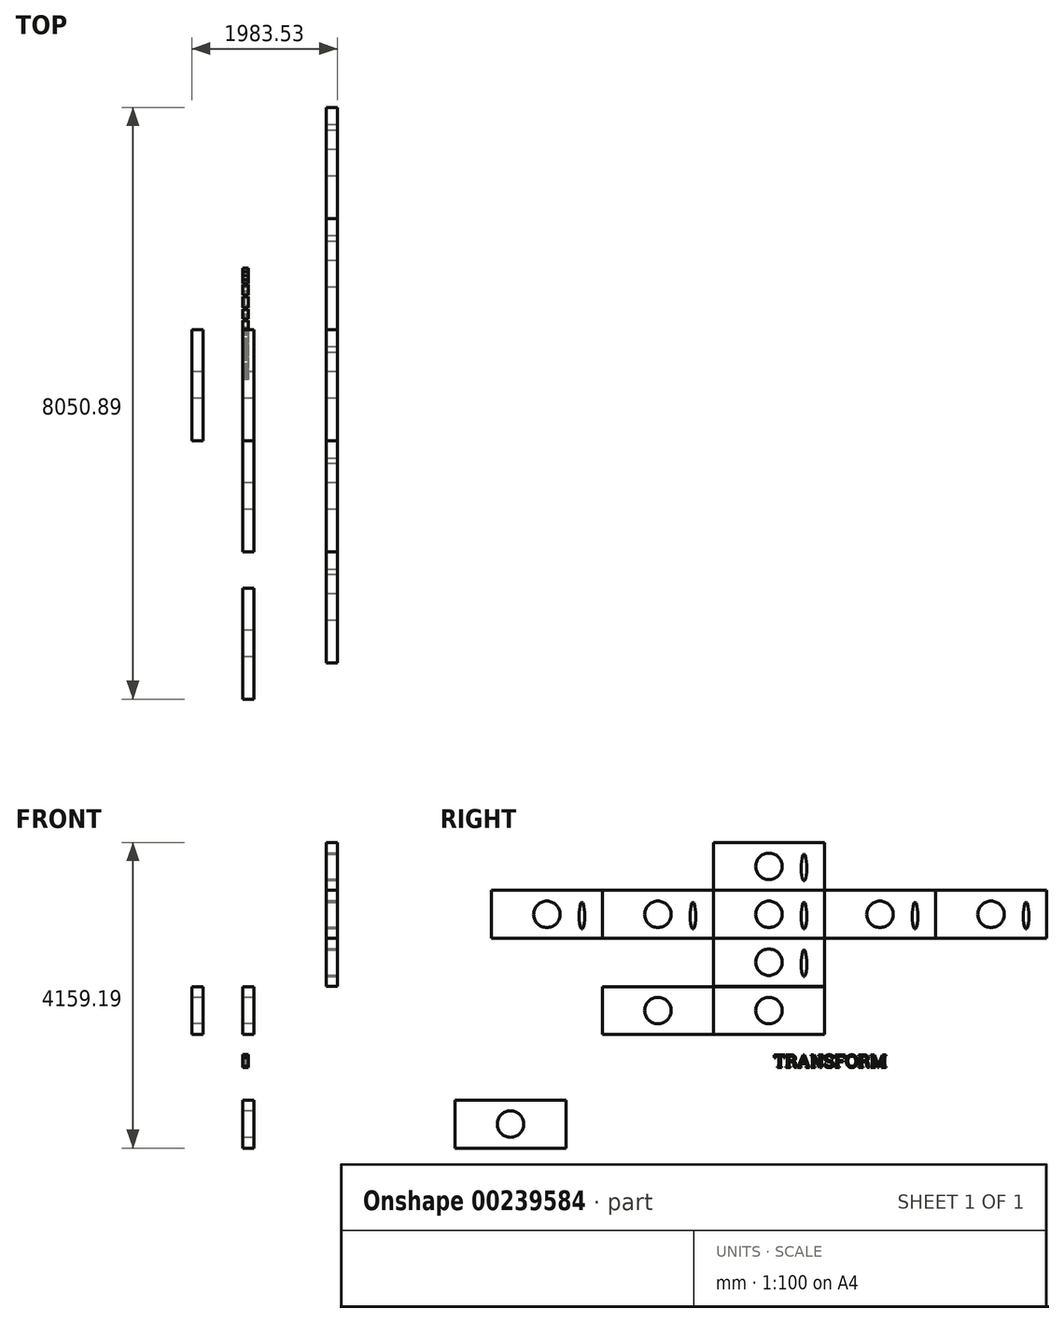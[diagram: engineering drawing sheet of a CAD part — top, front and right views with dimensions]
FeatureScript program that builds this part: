
annotation { "Feature Type Name" : "Feature", "Feature Type Description" : "" }
export const myFeature = defineFeature(function(context is Context, id is Id, definition is map)
    precondition{}
    {
        {
            var Q0;
            Q0=qCreatedBy(makeId("Right.planeOp"),FACE);
            var sketch = newSketch(context, id + "F0", { "sketchPlane" : qUnion([Q0])});
            skText(sketch, "E0", { "text": "TRANSFORM", "fontName": "RobotoSlab-Regular.ttf"});
            const initialGuessF0  = {"E0": [0.06953, -0.13173, 1, 0, 0.17393]};
            skSetInitialGuess(sketch, initialGuessF0);
            skSolve(sketch);
        }
        {
            var Q0;
            Q0=makeQuery(id+"F0.imprint","IMPRINT",FACE,{"disambiguationData":[TD([[makeQuery(id+"F0.imprint","IMPRINT",EDGE,{"derivedFrom":sQuery(id+"F0.wireOp",EDGE,"E0.sketch_text.stroke-154")}),1.0]])]});
            extrude(context, id + "F1", {"entities" : qUnion([Q0]), "depth" : 25.4 * mm});
        }
        {
            var Q0;
            Q0 = qSketchRegion(id + "F0", true);
            extrude(context, id + "F2", {"entities" : qUnion([Q0]), "operationType" : NewBodyOperationType.ADD, "depth" : 81.53 * mm});
        }
        {
            var Q0;
            Q0=qCreatedBy(makeId("Right.planeOp"),FACE);
            var sketch = newSketch(context, id + "F3", { "sketchPlane" : qUnion([Q0])});
            skLineSegment(sketch, "E1.bottom", {"start": v(755.67, 317.14) * mm, "end": v(-755.67, 317.14) * mm});
            skLineSegment(sketch, "E1.top", {"start": v(755.67, 969.35) * mm, "end": v(-755.67, 969.35) * mm});
            skLineSegment(sketch, "E1.left", {"start": v(755.67, 317.14) * mm, "end": v(755.67, 969.35) * mm});
            skLineSegment(sketch, "E1.right", {"start": v(-755.67, 317.14) * mm, "end": v(-755.67, 969.35) * mm});
            skPoint(sketch, "E1.middle", {"position": v(0, 643.24) * mm});
            skCircle(sketch, "E2", {"center": v(0, 643.24) * mm, "radius": 180.1 * mm});
            skSolve(sketch);
        }
        {
            var Q0;
            Q0 = qSketchRegion(id + "F3", true);
            extrude(context, id + "F14", {"entities" : qUnion([Q0]), "depth" : 152.9 * mm});
        }
        {
            var Q0;
            Q0=makeQuery(id+"F14.opExtrude","SWEPT_BODY",BODY,{"disambiguationData":[OSD([sQuery(id+"F3.wireOp",EDGE,"E1.bottom"),sQuery(id+"F3.wireOp",EDGE,"E1.top"),sQuery(id+"F3.wireOp",EDGE,"E1.left"),sQuery(id+"F3.wireOp",EDGE,"E1.right"),sQuery(id+"F3.wireOp",EDGE,"E2")])]});
            var Q1;
            Q1=sQuery(id+"F3.wireOp",EDGE,"E1.top");
            transform(context, id + "F4", {"entities" : qUnion([Q0]), "transformType" : TransformType.TRANSLATION_ENTITY, "oppositeDirectionEntity" : false, "transformLine" : qUnion([Q1]), "makeCopy" : true});
        }
        {
            var Q0;
            Q0=makeQuery(id+"F14.opExtrude","SWEPT_BODY",BODY,{"disambiguationData":[OSD([sQuery(id+"F3.wireOp",EDGE,"E1.bottom"),sQuery(id+"F3.wireOp",EDGE,"E1.top"),sQuery(id+"F3.wireOp",EDGE,"E1.left"),sQuery(id+"F3.wireOp",EDGE,"E1.right"),sQuery(id+"F3.wireOp",EDGE,"E2")])]});
            var Q1;
            Q1=sQuery(id+"F3.wireOp",EDGE,"E1.top");
            transform(context, id + "F15", {"entities" : qUnion([Q0]), "transformType" : TransformType.TRANSLATION_ENTITY, "oppositeDirectionEntity" : false, "transformLine" : qUnion([Q1]), "makeCopy" : true});
        }
        {
            var Q0;
            Q0=makeQuery(id+"F14.opExtrude","SWEPT_BODY",BODY,{"disambiguationData":[OSD([sQuery(id+"F3.wireOp",EDGE,"E1.bottom"),sQuery(id+"F3.wireOp",EDGE,"E1.top"),sQuery(id+"F3.wireOp",EDGE,"E1.left"),sQuery(id+"F3.wireOp",EDGE,"E1.right"),sQuery(id+"F3.wireOp",EDGE,"E2")])]});
            var Q1;
            Q1=makeQuery(id+"F14.opExtrude","CAP_EDGE",EDGE,{"disambiguationData":[OSD([sQuery(id+"F3.wireOp",EDGE,"E1.top")])],"isStart":false});
            transform(context, id + "F5", {"entities" : qUnion([Q0]), "transformType" : TransformType.TRANSLATION_3D, "dx" : -692.43 * mm, "dy" : 0 * mm, "dz" : 0 * mm, "makeCopy" : true});
        }
        {
            var Q0;
            Q0=makeQuery(id+"F14.opExtrude","SWEPT_BODY",BODY,{"disambiguationData":[OSD([sQuery(id+"F3.wireOp",EDGE,"E1.bottom"),sQuery(id+"F3.wireOp",EDGE,"E1.top"),sQuery(id+"F3.wireOp",EDGE,"E1.left"),sQuery(id+"F3.wireOp",EDGE,"E1.right"),sQuery(id+"F3.wireOp",EDGE,"E2")])]});
            transform(context, id + "F16", {"entities" : qUnion([Q0]), "transformType" : TransformType.TRANSLATION_3D, "dx" : 1138.2 * mm, "dy" : 0 * mm, "dz" : 1309.2 * mm, "makeCopy" : true});
        }
        {
            var Q0;
            Q0=makeQuery(id+"F16.opPattern","COPY",FACE,{"derivedFrom":makeQuery(id+"F14.opExtrude","CAP_FACE",FACE,{"disambiguationData":[OSD([sQuery(id+"F3.wireOp",EDGE,"E1.bottom"),sQuery(id+"F3.wireOp",EDGE,"E1.top"),sQuery(id+"F3.wireOp",EDGE,"E1.left"),sQuery(id+"F3.wireOp",EDGE,"E1.right"),sQuery(id+"F3.wireOp",EDGE,"E2")])],"isStart":false}),"instanceName":"1"});
            var sketch = newSketch(context, id + "F6", { "sketchPlane" : qUnion([Q0])});
            skEllipse(sketch, "E3", {"center": v(477.82, 1935.9) * mm, "majorRadius": 181.6 * mm, "minorRadius": 37.73 * mm, "majorAxis": v(0, 1)});
            skSolve(sketch);
        }
        {
            var Q0;
            Q0 = qSketchRegion(id + "F6", true);
            extrude(context, id + "F7", {"entities" : qUnion([Q0]), "operationType" : NewBodyOperationType.REMOVE, "endBound" : BoundingType.THROUGH_ALL, "oppositeDirection" : true, "depth" : 25.4 * mm});
        }
        {
            var Q0;
            Q0=makeQuery(id+"F16.opPattern","COPY",BODY,{"derivedFrom":makeQuery(id+"F14.opExtrude","SWEPT_BODY",BODY,{"disambiguationData":[OSD([sQuery(id+"F3.wireOp",EDGE,"E1.bottom"),sQuery(id+"F3.wireOp",EDGE,"E1.top"),sQuery(id+"F3.wireOp",EDGE,"E1.left"),sQuery(id+"F3.wireOp",EDGE,"E1.right"),sQuery(id+"F3.wireOp",EDGE,"E2")])]}),"instanceName":"1"});
            var Q1;
            Q1=makeQuery(id+"F16.opPattern","COPY",EDGE,{"derivedFrom":makeQuery(id+"F14.opExtrude","CAP_EDGE",EDGE,{"disambiguationData":[OSD([sQuery(id+"F3.wireOp",EDGE,"E1.top")])],"isStart":false}),"instanceName":"1"});
            transform(context, id + "F8", {"entities" : qUnion([Q0]), "transformType" : TransformType.TRANSLATION_ENTITY, "oppositeDirectionEntity" : false, "transformLine" : qUnion([Q1]), "makeCopy" : true});
        }
        {
            var Q0;
            Q0=makeQuery(id+"F4.opPattern","COPY",BODY,{"derivedFrom":makeQuery(id+"F14.opExtrude","SWEPT_BODY",BODY,{"disambiguationData":[OSD([sQuery(id+"F3.wireOp",EDGE,"E1.bottom"),sQuery(id+"F3.wireOp",EDGE,"E1.top"),sQuery(id+"F3.wireOp",EDGE,"E1.left"),sQuery(id+"F3.wireOp",EDGE,"E1.right"),sQuery(id+"F3.wireOp",EDGE,"E2")])]}),"instanceName":"1"});
            transform(context, id + "F9", {"entities" : qUnion([Q0]), "transformType" : TransformType.TRANSLATION_3D, "dx" : 0 * mm, "dy" : -2005.56 * mm, "dz" : -1545.56 * mm, "makeCopy" : true});
        }
        {
            var Q0;
            Q0=makeQuery(id+"F16.opPattern","COPY",BODY,{"derivedFrom":makeQuery(id+"F14.opExtrude","SWEPT_BODY",BODY,{"disambiguationData":[OSD([sQuery(id+"F3.wireOp",EDGE,"E1.bottom"),sQuery(id+"F3.wireOp",EDGE,"E1.top"),sQuery(id+"F3.wireOp",EDGE,"E1.left"),sQuery(id+"F3.wireOp",EDGE,"E1.right"),sQuery(id+"F3.wireOp",EDGE,"E2")])]}),"instanceName":"1"});
            var Q1;
            Q1=makeQuery(id+"F16.opPattern","COPY",EDGE,{"derivedFrom":makeQuery(id+"F14.opExtrude","CAP_EDGE",EDGE,{"disambiguationData":[OSD([sQuery(id+"F3.wireOp",EDGE,"E1.left")])],"isStart":false}),"instanceName":"1"});
            transform(context, id + "F17", {"entities" : qUnion([Q0]), "transformType" : TransformType.TRANSLATION_ENTITY, "oppositeDirectionEntity" : false, "transformLine" : qUnion([Q1]), "makeCopy" : true});
        }
        {
            var Q0;
            Q0=makeQuery(id+"F16.opPattern","COPY",BODY,{"derivedFrom":makeQuery(id+"F14.opExtrude","SWEPT_BODY",BODY,{"disambiguationData":[OSD([sQuery(id+"F3.wireOp",EDGE,"E1.bottom"),sQuery(id+"F3.wireOp",EDGE,"E1.top"),sQuery(id+"F3.wireOp",EDGE,"E1.left"),sQuery(id+"F3.wireOp",EDGE,"E1.right"),sQuery(id+"F3.wireOp",EDGE,"E2")])]}),"instanceName":"1"});
            var Q1;
            Q1=makeQuery(id+"F16.opPattern","COPY",EDGE,{"derivedFrom":makeQuery(id+"F14.opExtrude","CAP_EDGE",EDGE,{"disambiguationData":[OSD([sQuery(id+"F3.wireOp",EDGE,"E1.left")])],"isStart":false}),"instanceName":"1"});
            transform(context, id + "F10", {"entities" : qUnion([Q0]), "transformType" : TransformType.TRANSLATION_ENTITY, "oppositeDirectionEntity" : true, "transformLine" : qUnion([Q1]), "makeCopy" : true});
        }
        {
            var Q0;
            Q0=makeQuery(id+"F16.opPattern","COPY",BODY,{"derivedFrom":makeQuery(id+"F14.opExtrude","SWEPT_BODY",BODY,{"disambiguationData":[OSD([sQuery(id+"F3.wireOp",EDGE,"E1.bottom"),sQuery(id+"F3.wireOp",EDGE,"E1.top"),sQuery(id+"F3.wireOp",EDGE,"E1.left"),sQuery(id+"F3.wireOp",EDGE,"E1.right"),sQuery(id+"F3.wireOp",EDGE,"E2")])]}),"instanceName":"1"});
            var Q1;
            Q1=makeQuery(id+"F16.opPattern","COPY",EDGE,{"derivedFrom":makeQuery(id+"F14.opExtrude","CAP_EDGE",EDGE,{"disambiguationData":[OSD([sQuery(id+"F3.wireOp",EDGE,"E1.bottom")])],"isStart":false}),"instanceName":"1"});
            transform(context, id + "F11", {"entities" : qUnion([Q0]), "transformType" : TransformType.TRANSLATION_ENTITY, "oppositeDirectionEntity" : true, "transformLine" : qUnion([Q1]), "makeCopy" : true});
        }
        {
            var Q0;
            Q0=makeQuery(id+"F11.opPattern","COPY",BODY,{"derivedFrom":makeQuery(id+"F16.opPattern","COPY",BODY,{"derivedFrom":makeQuery(id+"F14.opExtrude","SWEPT_BODY",BODY,{"disambiguationData":[OSD([sQuery(id+"F3.wireOp",EDGE,"E1.bottom"),sQuery(id+"F3.wireOp",EDGE,"E1.top"),sQuery(id+"F3.wireOp",EDGE,"E1.left"),sQuery(id+"F3.wireOp",EDGE,"E1.right"),sQuery(id+"F3.wireOp",EDGE,"E2")])]}),"instanceName":"1"}),"instanceName":"1"});
            var Q1;
            Q1=makeQuery(id+"F11.opPattern","COPY",EDGE,{"derivedFrom":makeQuery(id+"F16.opPattern","COPY",EDGE,{"derivedFrom":makeQuery(id+"F14.opExtrude","CAP_EDGE",EDGE,{"disambiguationData":[OSD([sQuery(id+"F3.wireOp",EDGE,"E1.bottom")])],"isStart":false}),"instanceName":"1"}),"instanceName":"1"});
            transform(context, id + "F12", {"entities" : qUnion([Q0]), "transformType" : TransformType.TRANSLATION_ENTITY, "oppositeDirectionEntity" : true, "transformLine" : qUnion([Q1]), "makeCopy" : true});
        }
        {
            var Q0;
            Q0=makeQuery(id+"F8.opPattern","COPY",BODY,{"derivedFrom":makeQuery(id+"F16.opPattern","COPY",BODY,{"derivedFrom":makeQuery(id+"F14.opExtrude","SWEPT_BODY",BODY,{"disambiguationData":[OSD([sQuery(id+"F3.wireOp",EDGE,"E1.bottom"),sQuery(id+"F3.wireOp",EDGE,"E1.top"),sQuery(id+"F3.wireOp",EDGE,"E1.left"),sQuery(id+"F3.wireOp",EDGE,"E1.right"),sQuery(id+"F3.wireOp",EDGE,"E2")])]}),"instanceName":"1"}),"instanceName":"1"});
            var Q1;
            Q1=makeQuery(id+"F8.opPattern","COPY",EDGE,{"derivedFrom":makeQuery(id+"F16.opPattern","COPY",EDGE,{"derivedFrom":makeQuery(id+"F14.opExtrude","CAP_EDGE",EDGE,{"disambiguationData":[OSD([sQuery(id+"F3.wireOp",EDGE,"E1.bottom")])],"isStart":false}),"instanceName":"1"}),"instanceName":"1"});
            transform(context, id + "F13", {"entities" : qUnion([Q0]), "transformType" : TransformType.TRANSLATION_ENTITY, "oppositeDirectionEntity" : false, "transformLine" : qUnion([Q1]), "makeCopy" : true});
        }
    });
